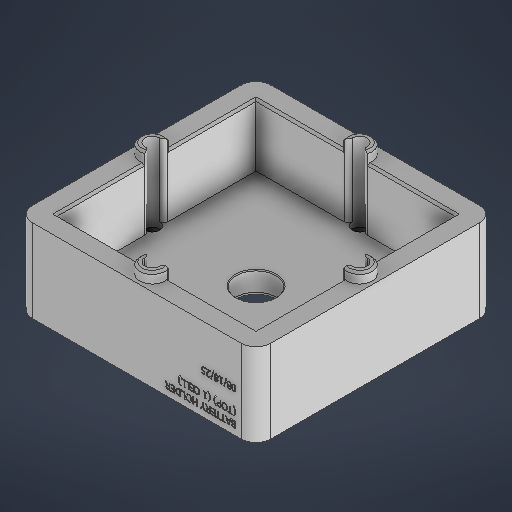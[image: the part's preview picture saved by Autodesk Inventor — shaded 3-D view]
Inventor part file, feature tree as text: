
AUTODESK INVENTOR PART (.ipt)
format: ipt  version: 2025 (Build 290162000, 162)  size: 890,368 bytes
history: native  units: in
note: dims shown in document units (in); Inventor stores cm internally (conversion verified against a paired STEP export)
features: sketch x6, extrude x4, hole x2, fillet x2, chamfer x2
ambient origin geometry x8: Origin, YZ Plane, XZ Plane, XY Plane, X Axis, Y Axis, Z Axis, Center Point
bodies: Solid1 (feature_tree)
feature tree (16):
  extrude  "Extrusion1"  Depth=4.5276in
  sketch  "Sketch4"  dims[d2=0.3937in d3=0.0in d48=3.7795in]
  extrude  "Extrusion3"  Depth=3.7795in
  hole  "Hole4"  [1 undecoded]
  hole  "Hole5"  [1 undecoded]
  extrude  "Extrusion4"  Depth=0.2362in
  fillet  "Fillet1"  Radius=0.4724in
  fillet  "Fillet2"  Radius=0.4724in
  chamfer  "Chamfer1"  Distance=0.4724in
  chamfer  "Chamfer2"  Distance=0.4724in
  extrude  "Extrusion5"  Depth=0.1969in TaperAngle=0.0deg
  sketch  "Sketch1"  dims[d0=4.5276in d1=4.5276in]
  sketch  "Sketch6"  dims[d49=3.7795in d174=1.1811in d175=0.0in]
  sketch  "Sketch Rectangular Pattern14"  dims[d186=1.1811in d188=1.9685in d189=1.1811in d191=1.9685in d194=0.2805in d195=0.2362in d196=0.5118in d197=0.2756in d198=0.0172in d199=0.315in d200=0.8108in d201=0.4724in d202=0.4724in d203=0.4724in d204=0.4724in d205=0.1969in d206=0.0in d207=0.2805in d208=0.0787in d209=0.0157in d210=0.0787in d211=45.0deg d212=0.0394in d213=0.0787in d214=45.0deg d215=0.0787in d216=0.0in d217=0.748in]
  sketch  "Sketch7"  dims[d176=0.7323in d177=0.2362in d178=0.748in d179=0.0787in d180=0.0172in d181=0.315in d182=0.8108in d183=3.937in]
  sketch  "Sketch8"  dims[d184=3.937in d185=0.2362in]
note: 2 required parameter values undecoded (feature->parameter linkage not recoverable at this tier; creation-order binding heuristic only, values carry confidence <= 0.55)
